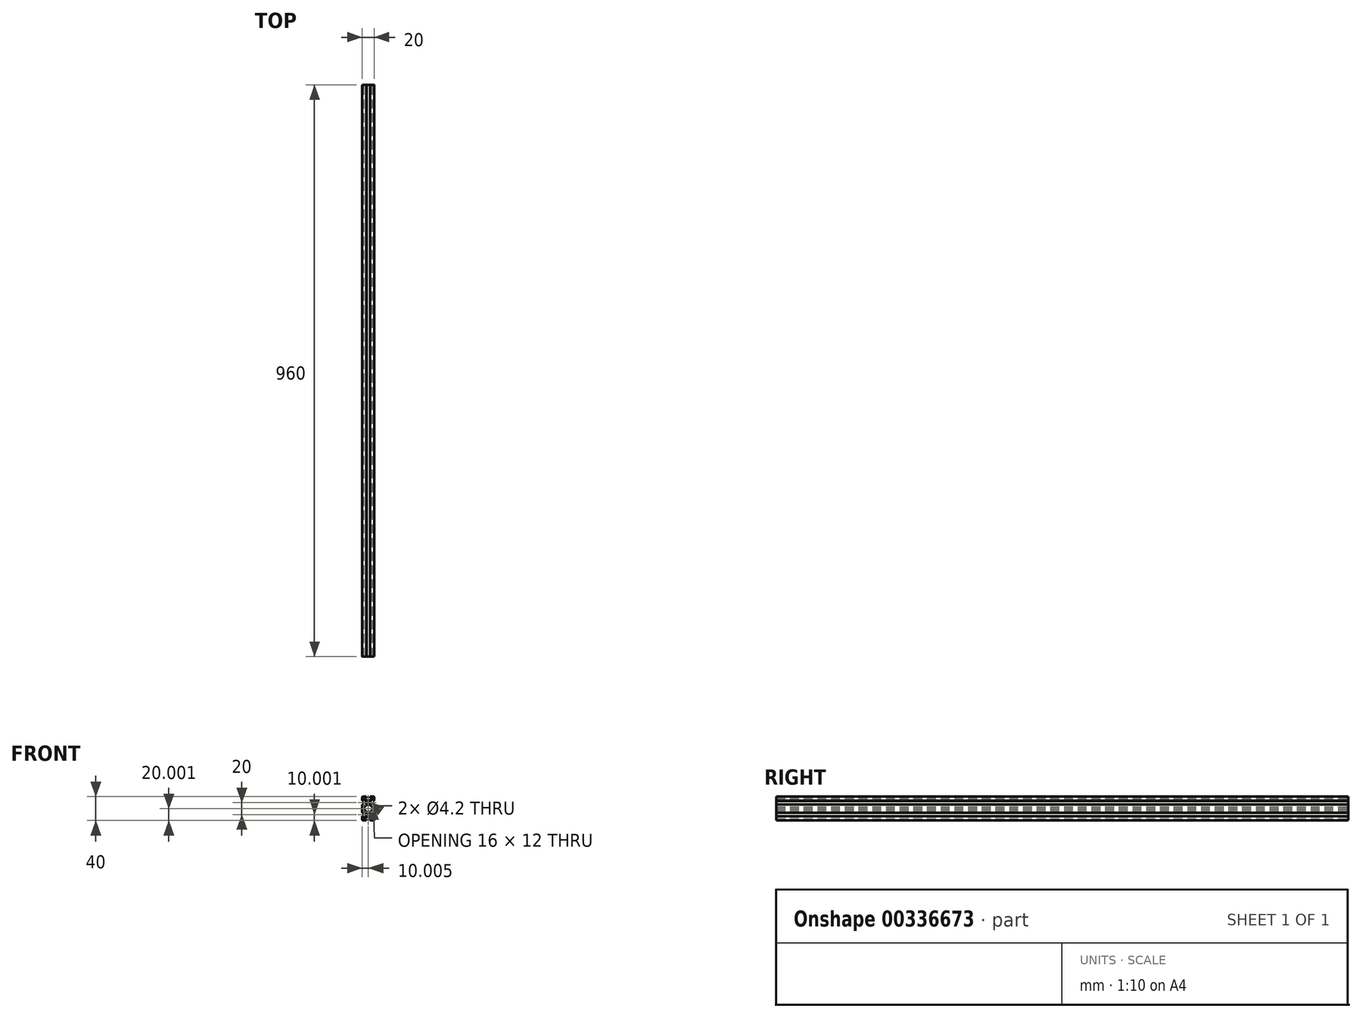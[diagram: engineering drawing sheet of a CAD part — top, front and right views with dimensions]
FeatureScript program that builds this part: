
annotation { "Feature Type Name" : "Feature", "Feature Type Description" : "" }
export const myFeature = defineFeature(function(context is Context, id is Id, definition is map)
    precondition{}
    {
        {
            var Q0;
            Q0=qCreatedBy(makeId("Front.planeOp"),FACE);
            var sketch = newSketch(context, id + "F0", { "sketchPlane" : qUnion([Q0])});
            skCircle(sketch, "E0", {"center": v(-0.06, -0.16) * mm, "radius": 2.1 * mm});
            skLineSegment(sketch, "E1.bottom", {"start": v(8.94, 9.84) * mm, "end": v(2.94, 9.84) * mm});
            skLineSegment(sketch, "E1.left", {"start": v(9.94, 8.84) * mm, "end": v(9.94, 2.84) * mm});
            skLineSegment(sketch, "E1.right", {"start": v(-10.06, 8.84) * mm, "end": v(-10.06, 2.84) * mm});
            skLineSegment(sketch, "E2.bottom", {"start": v(2.88, 3.84) * mm, "end": v(-3, 3.84) * mm});
            skLineSegment(sketch, "E2.top", {"start": v(2.88, -4.16) * mm, "end": v(-3, -4.16) * mm});
            skLineSegment(sketch, "E2.left", {"start": v(3.94, 2.78) * mm, "end": v(3.94, -3.1) * mm});
            skLineSegment(sketch, "E2.right", {"start": v(-4.06, 2.78) * mm, "end": v(-4.06, -3.1) * mm});
            skLineSegment(sketch, "E3.bottom", {"start": v(6.88, 7.84) * mm, "end": v(2.94, 7.84) * mm});
            skLineSegment(sketch, "E3.left", {"start": v(7.94, 6.78) * mm, "end": v(7.94, 2.84) * mm});
            skLineSegment(sketch, "E3.right", {"start": v(-8.06, 6.78) * mm, "end": v(-8.06, 2.84) * mm});
            skLineSegment(sketch, "E4.MirrorCS", {"start": v(-3.06, 9.84) * mm, "end": v(-3.06, 7.84) * mm});
            skLineSegment(sketch, "E5.MirrorCS", {"start": v(2.94, 9.84) * mm, "end": v(2.94, 7.84) * mm});
            skLineSegment(sketch, "E6", {"start": v(-10.06, 2.84) * mm, "end": v(-8.06, 2.84) * mm});
            skLineSegment(sketch, "E7.MirrorCS", {"start": v(-10.06, -3.16) * mm, "end": v(-8.06, -3.16) * mm});
            skLineSegment(sketch, "E8", {"start": v(7.94, 2.84) * mm, "end": v(9.94, 2.84) * mm});
            skLineSegment(sketch, "E9.MirrorCS", {"start": v(7.94, -3.16) * mm, "end": v(9.94, -3.16) * mm});
            skPoint(sketch, "E10", {"position": v(-8.06, -7.1) * mm});
            skPoint(sketch, "E11", {"position": v(6.88, 7.84) * mm});
            skPoint(sketch, "E12", {"position": v(-4.06, -3.1) * mm});
            skPoint(sketch, "E13", {"position": v(2.88, 3.84) * mm});
            skLineSegment(sketch, "E14", {"start": v(-8.06, -7.1) * mm, "end": v(-4.06, -3.1) * mm});
            skLineSegment(sketch, "E15", {"start": v(2.88, 3.84) * mm, "end": v(6.88, 7.84) * mm});
            skLineSegment(sketch, "E16.MirrorCS", {"start": v(-8.06, -9.22) * mm, "end": v(-3, -4.16) * mm});
            skLineSegment(sketch, "E17.1.0", {"start": v(7.94, -9.22) * mm, "end": v(2.88, -4.16) * mm});
            skLineSegment(sketch, "E17.2.0", {"start": v(7.94, 6.78) * mm, "end": v(3.94, 2.78) * mm});
            skLineSegment(sketch, "E17.3.0", {"start": v(-7, 7.84) * mm, "end": v(-3, 3.84) * mm});
            skLineSegment(sketch, "E18.1.0", {"start": v(7.94, -7.1) * mm, "end": v(3.94, -3.1) * mm});
            skLineSegment(sketch, "E18.2.0", {"start": v(6.88, 7.84) * mm, "end": v(2.88, 3.84) * mm});
            skLineSegment(sketch, "E18.3.0", {"start": v(-8.06, 6.78) * mm, "end": v(-4.06, 2.78) * mm});
            skLineSegment(sketch, "E19.trimOffspring", {"start": v(-3.06, 7.84) * mm, "end": v(-7, 7.84) * mm});
            skLineSegment(sketch, "E20.trimOffspring", {"start": v(-3.06, 9.84) * mm, "end": v(-9.06, 9.84) * mm});
            skLineSegment(sketch, "E21.trimOffspring", {"start": v(7.94, -3.16) * mm, "end": v(7.94, -7.1) * mm});
            skLineSegment(sketch, "E22.trimOffspring", {"start": v(9.94, -3.16) * mm, "end": v(9.94, -10.16) * mm});
            skLineSegment(sketch, "E23.trimOffspring", {"start": v(-10.06, -3.16) * mm, "end": v(-10.06, -10.16) * mm});
            skLineSegment(sketch, "E24.trimOffspring", {"start": v(-8.06, -3.16) * mm, "end": v(-8.06, -7.1) * mm});
            skArc(sketch, "E25.filletArc", {"start": v(9.94, 8.84) * mm, "mid": v(9.65, 9.55) * mm, "end": v(8.94, 9.84) * mm});
            skArc(sketch, "E26.filletArc", {"start": v(-9.06, 9.84) * mm, "mid": v(-9.76, 9.55) * mm, "end": v(-10.06, 8.84) * mm});
            skLineSegment(sketch, "E27", {"start": v(-8.06, -9.22) * mm, "end": v(-8.06, -10.16) * mm});
            skLineSegment(sketch, "E28", {"start": v(7.94, -9.22) * mm, "end": v(7.94, -10.16) * mm});
            skPoint(sketch, "E29.MirrorP", {"position": v(-0.06, -20.16) * mm});
            skArc(sketch, "E30.MirrorCS", {"start": v(-9.06, -30.16) * mm, "mid": v(-9.76, -29.87) * mm, "end": v(-10.06, -29.16) * mm});
            skLineSegment(sketch, "E31.MirrorCS", {"start": v(-8.06, -11.1) * mm, "end": v(-8.06, -10.16) * mm});
            skLineSegment(sketch, "E32.MirrorCS", {"start": v(6.88, -28.16) * mm, "end": v(2.88, -24.16) * mm});
            skLineSegment(sketch, "E33.MirrorCS", {"start": v(7.94, -11.1) * mm, "end": v(7.94, -10.16) * mm});
            skLineSegment(sketch, "E34.MirrorCS", {"start": v(2.88, -24.16) * mm, "end": v(6.88, -28.16) * mm});
            skLineSegment(sketch, "E35.MirrorCS", {"start": v(2.88, -24.16) * mm, "end": v(-3, -24.16) * mm});
            skLineSegment(sketch, "E36.MirrorCS", {"start": v(2.94, -30.16) * mm, "end": v(2.94, -28.16) * mm});
            skLineSegment(sketch, "E37.MirrorCS", {"start": v(-7, -28.16) * mm, "end": v(-3, -24.16) * mm});
            skLineSegment(sketch, "E38.MirrorCS", {"start": v(-8.06, -27.1) * mm, "end": v(-8.06, -23.16) * mm});
            skLineSegment(sketch, "E39.MirrorCS", {"start": v(7.94, -23.16) * mm, "end": v(9.94, -23.16) * mm});
            skLineSegment(sketch, "E40.MirrorCS", {"start": v(-10.06, -17.16) * mm, "end": v(-8.06, -17.16) * mm});
            skCircle(sketch, "E41.MirrorC", {"center": v(-0.06, -20.16) * mm, "radius": 2.1 * mm});
            skLineSegment(sketch, "E42.MirrorCS", {"start": v(8.94, -30.16) * mm, "end": v(2.94, -30.16) * mm});
            skLineSegment(sketch, "E43.MirrorCS", {"start": v(-8.06, -13.22) * mm, "end": v(-4.06, -17.22) * mm});
            skLineSegment(sketch, "E44.MirrorCS", {"start": v(-4.06, -23.1) * mm, "end": v(-4.06, -17.22) * mm});
            skPoint(sketch, "E45.MirrorP", {"position": v(-8.06, -13.22) * mm});
            skLineSegment(sketch, "E46.MirrorCS", {"start": v(7.94, -27.1) * mm, "end": v(3.94, -23.1) * mm});
            skLineSegment(sketch, "E47.MirrorCS", {"start": v(-3.06, -28.16) * mm, "end": v(-7, -28.16) * mm});
            skLineSegment(sketch, "E48.MirrorCS", {"start": v(7.94, -17.16) * mm, "end": v(7.94, -13.22) * mm});
            skLineSegment(sketch, "E49.MirrorCS", {"start": v(7.94, -17.16) * mm, "end": v(9.94, -17.16) * mm});
            skPoint(sketch, "E50.MirrorP", {"position": v(-4.06, -17.22) * mm});
            skLineSegment(sketch, "E51.MirrorCS", {"start": v(9.94, -17.16) * mm, "end": v(9.94, -10.16) * mm});
            skLineSegment(sketch, "E52.MirrorCS", {"start": v(-8.06, -11.1) * mm, "end": v(-3, -16.16) * mm});
            skLineSegment(sketch, "E53.MirrorCS", {"start": v(-8.06, -27.1) * mm, "end": v(-4.06, -23.1) * mm});
            skLineSegment(sketch, "E54.MirrorCS", {"start": v(7.94, -13.22) * mm, "end": v(3.94, -17.22) * mm});
            skLineSegment(sketch, "E55.MirrorCS", {"start": v(-10.06, -17.16) * mm, "end": v(-10.06, -10.16) * mm});
            skLineSegment(sketch, "E56.MirrorCS", {"start": v(-3.06, -30.16) * mm, "end": v(-3.06, -28.16) * mm});
            skLineSegment(sketch, "E57.MirrorCS", {"start": v(6.88, -28.16) * mm, "end": v(2.94, -28.16) * mm});
            skLineSegment(sketch, "E58.MirrorCS", {"start": v(7.94, -11.1) * mm, "end": v(2.88, -16.16) * mm});
            skLineSegment(sketch, "E59.MirrorCS", {"start": v(3.94, -23.1) * mm, "end": v(3.94, -17.22) * mm});
            skLineSegment(sketch, "E60.MirrorCS", {"start": v(-3.06, -30.16) * mm, "end": v(-9.06, -30.16) * mm});
            skLineSegment(sketch, "E61.MirrorCS", {"start": v(-8.06, -17.16) * mm, "end": v(-8.06, -13.22) * mm});
            skLineSegment(sketch, "E62.MirrorCS", {"start": v(2.88, -16.16) * mm, "end": v(-3, -16.16) * mm});
            skLineSegment(sketch, "E63.MirrorCS", {"start": v(-10.06, -29.16) * mm, "end": v(-10.06, -23.16) * mm});
            skLineSegment(sketch, "E64.MirrorCS", {"start": v(7.94, -27.1) * mm, "end": v(7.94, -23.16) * mm});
            skPoint(sketch, "E65.MirrorP", {"position": v(6.88, -28.16) * mm});
            skPoint(sketch, "E66.MirrorP", {"position": v(2.88, -24.16) * mm});
            skLineSegment(sketch, "E67.MirrorCS", {"start": v(9.94, -29.16) * mm, "end": v(9.94, -23.16) * mm});
            skLineSegment(sketch, "E68.MirrorCS", {"start": v(-10.06, -23.16) * mm, "end": v(-8.06, -23.16) * mm});
            skArc(sketch, "E69.MirrorCS", {"start": v(9.94, -29.16) * mm, "mid": v(9.65, -29.87) * mm, "end": v(8.94, -30.16) * mm});
            skSolve(sketch);
        }
        {
            var Q0;
            Q0 = qSketchRegion(id + "F0", true);
            extrude(context, id + "F1", {"entities" : qUnion([Q0]), "depth" : 960 * mm});
        }
    });
